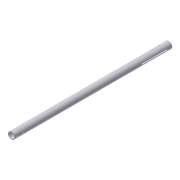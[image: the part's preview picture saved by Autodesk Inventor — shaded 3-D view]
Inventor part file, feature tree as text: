
AUTODESK INVENTOR PART (.ipt)
format: ipt  version: unknown  size: 193,536 bytes
history: native  units: in
note: dims shown in document units (in); Inventor stores cm internally (conversion verified against a paired STEP export)
features: extrude x3, sketch x3, projected_geometry x2, plane x1, other x1
ambient origin geometry x8: Origin, YZ Plane, XZ Plane, XY Plane, X Axis, Y Axis, Z Axis, Center Point
feature tree (10):
  extrude  "Extrusion1"  Depth=1.375in
  plane  "Work Plane1"
  extrude  "Extrusion2"  TaperAngle=0.0deg  [1 undecoded]
  extrude  "Extrusion3"  Depth=1.5in
  sketch  "Sketch1"  dims[d0=1.656in d1=1.375in]
  other  "Work Axis1"
  sketch  "Sketch2"  dims[d2=38.0in d3=0.0in d4=0.0in]
  projected_geometry  "Projected Loop1"
  projected_geometry  "Projected Loop2"
  sketch  "Sketch3"  dims[d5=0.5625in d6=1.5in d7=0.25in d8=38.0in d9=0.0in d10=0.25in d11=0.25in d12=0.125in d13=0.25in d14=6.0in d15=1.25in d16=38.0in d17=0.0in]
note: 1 required parameter value undecoded (feature->parameter linkage not recoverable at this tier; creation-order binding heuristic only, values carry confidence <= 0.55)
